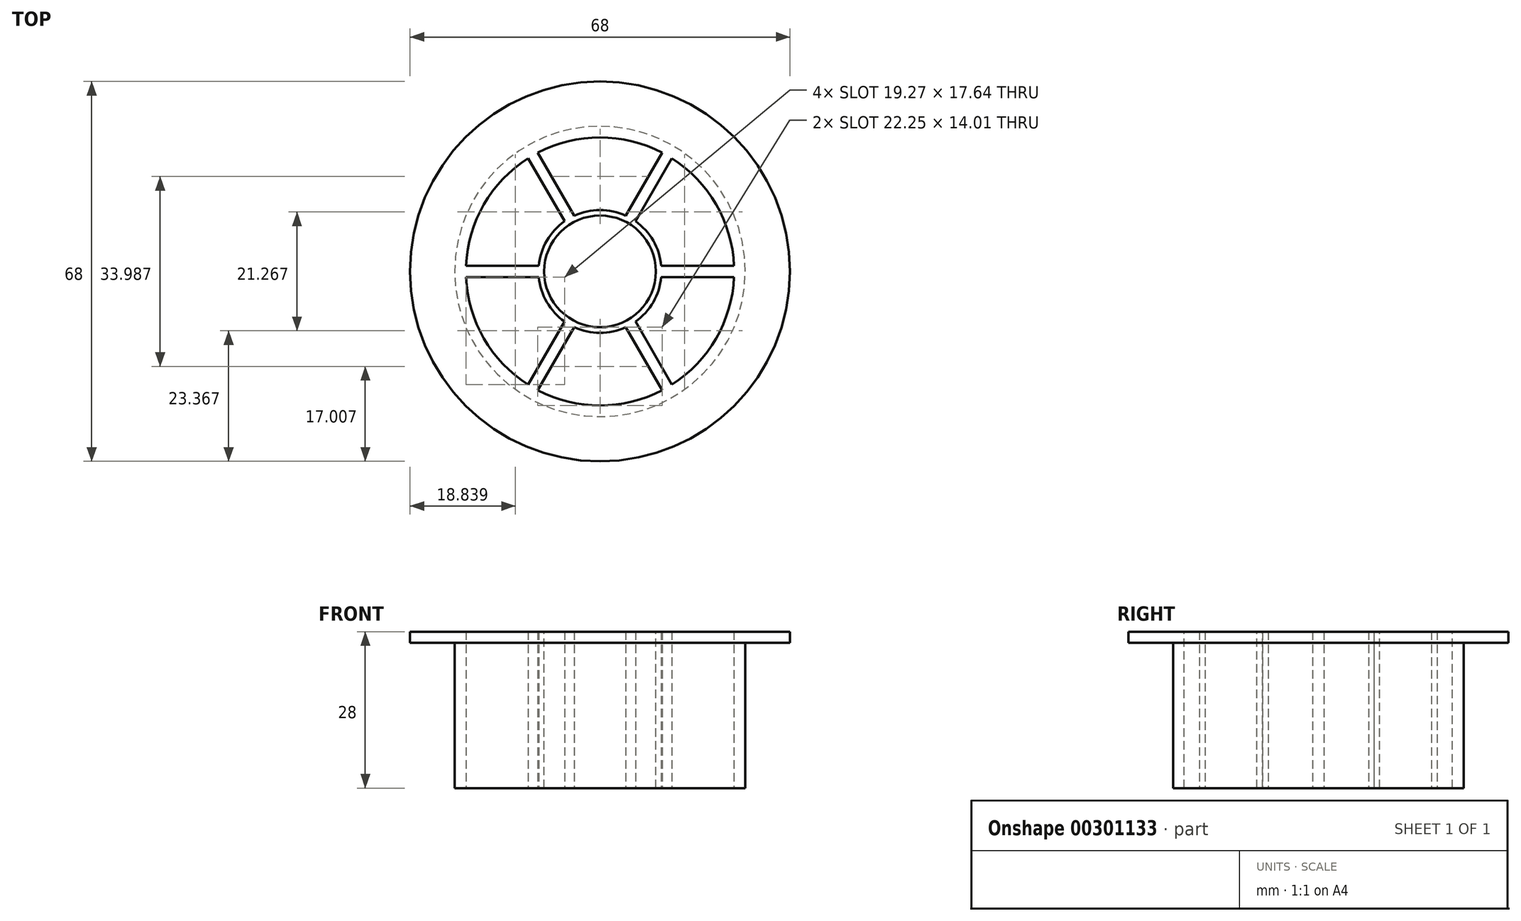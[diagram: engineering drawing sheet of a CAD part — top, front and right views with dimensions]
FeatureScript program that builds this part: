
annotation { "Feature Type Name" : "Feature", "Feature Type Description" : "" }
export const myFeature = defineFeature(function(context is Context, id is Id, definition is map)
    precondition{}
    {
        {
            var Q0;
            Q0=qCreatedBy(makeId("Front.planeOp"),FACE);
            var sketch = newSketch(context, id + "F0", { "sketchPlane" : qUnion([Q0])});
            skLineSegment(sketch, "E0", {"start": v(24, 0) * mm, "end": v(34, 0) * mm});
            skLineSegment(sketch, "E1", {"start": v(34, 0) * mm, "end": v(34, -2) * mm});
            skLineSegment(sketch, "E2", {"start": v(34, -2) * mm, "end": v(26, -2) * mm});
            skLineSegment(sketch, "E3", {"start": v(26, -2) * mm, "end": v(26, -28) * mm});
            skLineSegment(sketch, "E4", {"start": v(26, -28) * mm, "end": v(24, -28) * mm});
            skLineSegment(sketch, "E5", {"start": v(24, -28) * mm, "end": v(24, 0) * mm});
            skLineSegment(sketch, "E6", {"start": v(0, 29.7) * mm, "end": v(0, -37.38) * mm, "construction": true});
            skSolve(sketch);
        }
        {
            var Q0;
            Q0=makeQuery(id+"F0.imprint","IMPRINT",FACE,{"disambiguationData":[TD([[makeQuery(id+"F0.imprint","IMPRINT",EDGE,{"derivedFrom":sQuery(id+"F0.wireOp",EDGE,"E0")}),-1.0]])]});
            var Q1;
            Q1=sQuery(id+"F0.wireOp",EDGE,"E6");
            revolve(context, id + "F1", {"entities" : qUnion([Q0]), "axis" : qUnion([Q1]), "revolveType" : RevolveType.FULL});
        }
        {
            var Q0;
            Q0=qCreatedBy(makeId("Top.planeOp"),FACE);
            var sketch = newSketch(context, id + "F2", { "sketchPlane" : qUnion([Q0])});
            skCircle(sketch, "E7", {"center": v(0, 0) * mm, "radius": 10 * mm});
            skCircle(sketch, "E8", {"center": v(0, 0) * mm, "radius": 11 * mm});
            skSolve(sketch);
        }
        {
            var Q0;
            Q0=makeQuery(id+"F2.imprint","IMPRINT",FACE,{"disambiguationData":[TD([[makeQuery(id+"F2.imprint","IMPRINT",EDGE,{"derivedFrom":sQuery(id+"F2.wireOp",EDGE,"E7")}),-1.0]])]});
            var Q1;
            Q1=makeQuery(id+"F1.opRevolve","SWEPT_FACE",FACE,{"disambiguationData":[OSD([sQuery(id+"F0.wireOp",EDGE,"E4")])]});
            extrude(context, id + "F3", {"entities" : qUnion([Q0]), "endBound" : BoundingType.UP_TO_SURFACE, "oppositeDirection" : true, "endBoundEntityFace" : qUnion([Q1]), "depth" : 25 * mm});
        }
        {
            var Q0;
            Q0=makeQuery(id+"F1.opRevolve","SWEPT_FACE",FACE,{"disambiguationData":[OSD([sQuery(id+"F0.wireOp",EDGE,"E4")])]});
            var sketch = newSketch(context, id + "F4", { "sketchPlane" : qUnion([Q0])});
            skArc(sketch, "E9.0", {"start": v(-23.98, 1) * mm, "mid": v(-24, 0) * mm, "end": v(-23.98, -1) * mm});
            skArc(sketch, "E9.1", {"start": v(-10.95, 1) * mm, "mid": v(-11, 0) * mm, "end": v(-10.95, -1) * mm});
            skLineSegment(sketch, "E10", {"start": v(-23.98, 1) * mm, "end": v(-10.95, 1) * mm});
            skLineSegment(sketch, "E11", {"start": v(-23.98, -1) * mm, "end": v(-10.95, -1) * mm});
            skLineSegment(sketch, "E12.1.0", {"start": v(-12.86, -20.27) * mm, "end": v(-6.34, -8.99) * mm});
            skArc(sketch, "E12.1.1", {"start": v(-6.34, -8.99) * mm, "mid": v(-5.5, -9.53) * mm, "end": v(-4.61, -9.99) * mm});
            skLineSegment(sketch, "E12.1.2", {"start": v(-11.12, -21.27) * mm, "end": v(-4.61, -9.99) * mm});
            skArc(sketch, "E12.1.3", {"start": v(-12.86, -20.27) * mm, "mid": v(-12, -20.78) * mm, "end": v(-11.12, -21.27) * mm});
            skLineSegment(sketch, "E12.2.0", {"start": v(11.12, -21.27) * mm, "end": v(4.61, -9.99) * mm});
            skArc(sketch, "E12.2.1", {"start": v(4.61, -9.99) * mm, "mid": v(5.5, -9.53) * mm, "end": v(6.34, -8.99) * mm});
            skLineSegment(sketch, "E12.2.2", {"start": v(12.86, -20.27) * mm, "end": v(6.34, -8.99) * mm});
            skArc(sketch, "E12.2.3", {"start": v(11.12, -21.27) * mm, "mid": v(12, -20.78) * mm, "end": v(12.86, -20.27) * mm});
            skLineSegment(sketch, "E12.3.0", {"start": v(23.98, -1) * mm, "end": v(10.95, -1) * mm});
            skArc(sketch, "E12.3.1", {"start": v(10.95, -1) * mm, "mid": v(11, 0) * mm, "end": v(10.95, 1) * mm});
            skLineSegment(sketch, "E12.3.2", {"start": v(23.98, 1) * mm, "end": v(10.95, 1) * mm});
            skArc(sketch, "E12.3.3", {"start": v(23.98, -1) * mm, "mid": v(24, 0) * mm, "end": v(23.98, 1) * mm});
            skLineSegment(sketch, "E12.4.0", {"start": v(12.86, 20.27) * mm, "end": v(6.34, 8.99) * mm});
            skArc(sketch, "E12.4.1", {"start": v(6.34, 8.99) * mm, "mid": v(5.5, 9.53) * mm, "end": v(4.61, 9.99) * mm});
            skLineSegment(sketch, "E12.4.2", {"start": v(11.12, 21.27) * mm, "end": v(4.61, 9.99) * mm});
            skArc(sketch, "E12.4.3", {"start": v(12.86, 20.27) * mm, "mid": v(12, 20.78) * mm, "end": v(11.12, 21.27) * mm});
            skLineSegment(sketch, "E12.5.0", {"start": v(-11.12, 21.27) * mm, "end": v(-4.61, 9.99) * mm});
            skArc(sketch, "E12.5.1", {"start": v(-4.61, 9.99) * mm, "mid": v(-5.5, 9.53) * mm, "end": v(-6.34, 8.99) * mm});
            skLineSegment(sketch, "E12.5.2", {"start": v(-12.86, 20.27) * mm, "end": v(-6.34, 8.99) * mm});
            skArc(sketch, "E12.5.3", {"start": v(-11.12, 21.27) * mm, "mid": v(-12, 20.78) * mm, "end": v(-12.86, 20.27) * mm});
            skSolve(sketch);
        }
        {
            var Q0;
            Q0 = qSketchRegion(id + "F4", true);
            var Q1;
            Q1=makeQuery(id+"F1.opRevolve","SWEPT_FACE",FACE,{"disambiguationData":[OSD([sQuery(id+"F0.wireOp",EDGE,"E0")])]});
            extrude(context, id + "F5", {"entities" : qUnion([Q0]), "operationType" : NewBodyOperationType.ADD, "endBound" : BoundingType.UP_TO_SURFACE, "oppositeDirection" : true, "endBoundEntityFace" : qUnion([Q1]), "depth" : 25 * mm});
        }
    });
